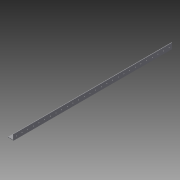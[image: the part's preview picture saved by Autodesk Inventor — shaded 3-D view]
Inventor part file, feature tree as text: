
AUTODESK INVENTOR PART (.ipt)
format: ipt  version: 2015 SP1 (Build 190203100, 203)  size: 144,896 bytes
history: native  units: in
note: dims shown in document units (in); Inventor stores cm internally (conversion verified against a paired STEP export)
features: sketch x3, hole x2, pattern_linear x2, projected_geometry x2, extrude x1
ambient origin geometry x8: Origin, YZ Plane, XZ Plane, XY Plane, X Axis, Y Axis, Z Axis, Center Point
bodies: Solid1 (feature_tree)
feature tree (10):
  extrude  "Extrusion1"  Depth=0.09in
  hole  "Hole1"  [1 undecoded]
  pattern_linear  "Rectangular Pattern1"  Spacing1=0.5in  [1 undecoded]
  hole  "Hole2"  [1 undecoded]
  pattern_linear  "Rectangular Pattern2"  Count1=28 Spacing1=1.0in
  sketch  "Sketch1"  dims[d0=1.0in d1=0.09in]
  sketch  "Sketch2"  dims[d2=0.09in d3=1.0in]
  projected_geometry  "Projected Loop1"
  sketch  "Sketch3"  dims[d4=28.0in d5=0.0in d6=0.5in d7=0.5in d8=0.1562in d9=0.75in d10=0.375in d11=0.25in d12=0.5635in d13=1.0in d14=0.8108in d15=11.0236in d17=1.0in d18=0.5in d19=0.5in d20=0.1562in d21=0.75in d22=0.375in d23=0.25in d24=0.5635in d25=1.0in d26=0.8108in d27=11.0236in d29=1.0in]
  projected_geometry  "Projected Loop2"
note: 3 required parameter values undecoded (feature->parameter linkage not recoverable at this tier; creation-order binding heuristic only, values carry confidence <= 0.55)
